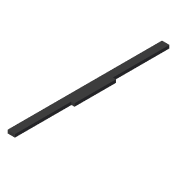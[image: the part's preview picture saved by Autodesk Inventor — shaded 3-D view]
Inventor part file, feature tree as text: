
AUTODESK INVENTOR PART (.ipt)
format: ipt  version: 2020 (Build 240168000, 168)  size: 87,040 bytes
history: native  units: mm
features: extrude x1, sketch x1
ambient origin geometry x8: Origin, YZ Plane, XZ Plane, XY Plane, X Axis, Y Axis, Z Axis, Center Point
bodies: Solid1 (feature_tree)
feature tree (2):
  extrude  "Extrusion1"  Depth=3.0mm
  sketch  "Sketch1"  dims[d0=150.0mm d1=3.0mm d2=40.0mm d3=7.0mm d4=3.0mm d5=0.0mm]
